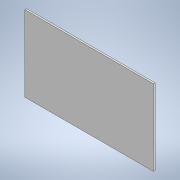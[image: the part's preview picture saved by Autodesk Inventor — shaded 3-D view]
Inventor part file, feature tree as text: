
AUTODESK INVENTOR PART (.ipt)
format: ipt  version: 2021 (Build 250183000, 183)  size: 96,768 bytes
history: native  units: in
note: dims shown in document units (in); Inventor stores cm internally (conversion verified against a paired STEP export)
features: extrude x1, sketch x1
ambient origin geometry x8: Origin, YZ Plane, XZ Plane, XY Plane, X Axis, Y Axis, Z Axis, Center Point
bodies: Solid1 (feature_tree)
feature tree (2):
  extrude  "Extrusion1"  Depth=1.7717in
  sketch  "Sketch1"  dims[d0=3.0in d1=1.7717in d2=0.0394in d3=0.0in]
